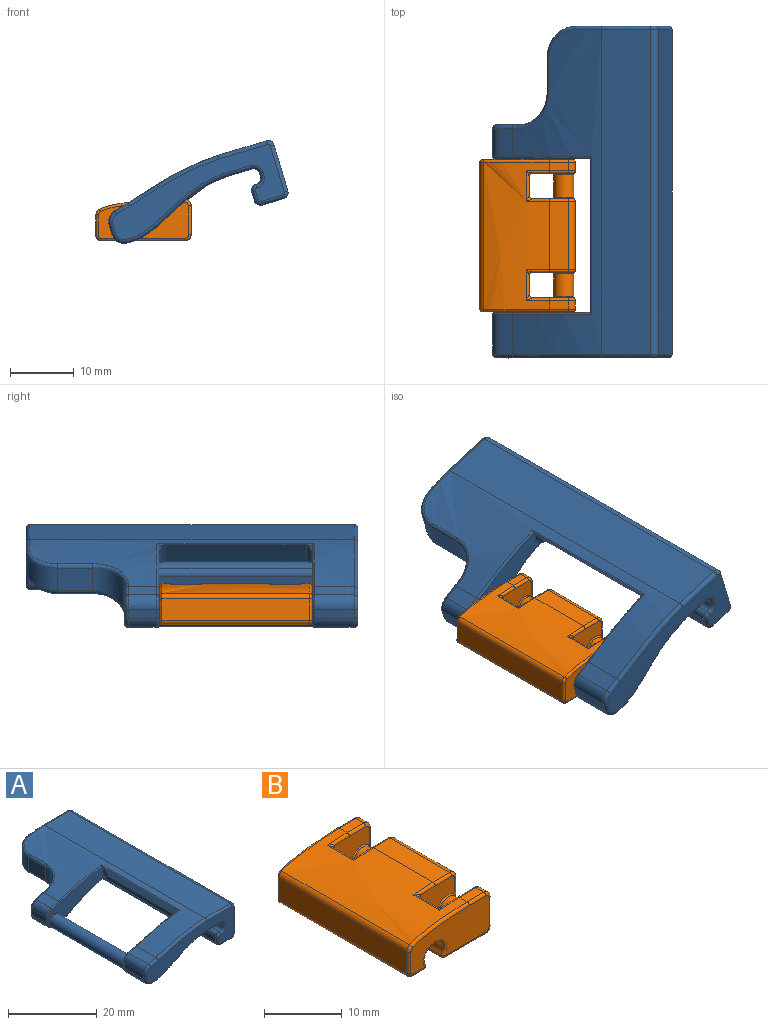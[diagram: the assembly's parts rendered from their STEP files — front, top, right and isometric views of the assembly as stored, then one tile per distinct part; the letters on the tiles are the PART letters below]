
ASSEMBLY  parts=2 mates=1
PART A: 118 faces, bbox 30x52.3x9.5 mm
  f0: plane 2.15x0.64mm, normal (-1,0,0), area 0.4mm2, adj f21,f24,f84,f85
  f1: extruded ~51.05x15.64mm, area 359.3mm2, adj f3,f12,f13,f38,f39,f41,f43,f45
  f2: extruded ~51.05x17mm, area 362.6mm2, adj f4,f15,f16,f50,f52,f54,f56,f58
  f3: plane 4.5x2.38mm, normal (-0.26,0,0.97), area 11.1mm2, adj f1,f5,f40,f88
  f4: plane 4.69x1mm, normal (0,0,-1), area 4.6mm2, adj f2,f6,f48,f98
  f5: cylinder r=2mm len=4.5mm, axis (0,-1,0), area 11.8mm2, adj f3,f17,f42,f90
  f6: cylinder r=2mm len=4.63mm, axis (0,1,0), area 14.2mm2, adj f4,f17,f46,f94,f96
  f7: plane 12.9x8.3mm, normal (0,1,0), area 50.6mm2, adj f37,f45,f47,f49,f51,f53,f55,f57
  f8: plane 51.05x0.5mm, normal (-1,0,0), area 25.5mm2, adj f29,f33,f64,f81
  f9: plane 51.05x1.4mm, normal (-1,0,0), area 71.5mm2, adj f28,f30,f59,f80
  f10: plane 51.05x3.5mm, normal (0,0,-1), area 178.7mm2, adj f30,f31,f55,f76
  f11: plane 51.05x7.5mm, normal (1,0,0), area 382.9mm2, adj f31,f32,f51,f72
  f12: plane 51.05x8mm, normal (0,0,1), area 408.4mm2, adj f1,f32,f47,f68
  f13: plane 6.25x2.38mm, normal (-0.26,0,0.97), area 15.4mm2, adj f1,f18,f65,f87
  f14: plane 6.25x1.47mm, normal (-1,0,0), area 9.2mm2, adj f18,f19,f69,f91
  f15: plane 6.44x1mm, normal (0,0,-1), area 6.4mm2, adj f2,f19,f73,f97
  f16: plane 51.05x4mm, normal (0,0,-1), area 204.2mm2, adj f2,f33,f60,f77
  f17: plane 4.5x1.47mm, normal (-1,0,0), area 6.6mm2, adj f5,f6,f44,f92
  f18: cylinder r=2mm len=6.25mm, axis (0,-1,0), area 16.4mm2, adj f13,f14,f67,f89
  f19: cylinder r=2mm len=6.38mm, axis (0,1,0), area 19.7mm2, adj f14,f15,f71,f93,f95
  f20: plane 2.15x0.64mm, normal (-1,0,0), area 0.4mm2, adj f22,f25,f84,f86
  f21: plane 17.65x8.41mm, normal (0,1,0), area 66.1mm2, adj f0,f24,f85,f87,f89,f91,f93,f101
  f22: plane 17.65x8.41mm, normal (0,-1,0), area 66.1mm2, adj f20,f25,f86,f88,f90,f92,f94,f102
  f23: plane 22.2x3.18mm, normal (-0.9,0,-0.43), area 78.3mm2, adj f24,f25,f84,f105
  f24: cylinder r=1mm len=3.61mm, axis (-0.43,0,0.9), area 4mm2, adj f0,f21,f23,f84,f103
  f25: cylinder r=1mm len=3.61mm, axis (-0.43,0,0.9), area 4mm2, adj f20,f22,f23,f84,f104
  f26: cylinder r=1.7mm len=24.12mm, axis (0,-1,0), area 255.7mm2, adj f106,f107,f108,f109,f110,f111,f112,f113
  f27: plane 27.3x8.3mm, normal (0,-1,0), area 108.1mm2, adj f65,f66,f67,f68,f69,f70,f71,f72
  f28: cylinder r=1mm len=51.05mm, axis (0,1,0), area 80.2mm2, adj f9,f29,f61,f82
  f29: cylinder r=1mm len=51.05mm, axis (0,-1,0), area 80.2mm2, adj f8,f28,f63,f83
  f30: cylinder r=1mm len=51.05mm, axis (0,1,0), area 80.2mm2, adj f9,f10,f57,f78
  f31: cylinder r=1mm len=51.05mm, axis (0,1,0), area 80.2mm2, adj f10,f11,f53,f74
  f32: cylinder r=1mm len=51.05mm, axis (0,1,0), area 80.2mm2, adj f11,f12,f49,f70
  f33: cylinder r=1mm len=51.05mm, axis (0,-1,0), area 80.2mm2, adj f8,f16,f62,f79
  f34: plane 5.13x4.4mm, normal (0,1,0), area 19mm2, adj f36,f38,f40,f42,f44,f46,f48,f50
  f35: plane 5.5x3.74mm, normal (-1,0,0), area 20.5mm2, adj f36,f37,f41,f54
  f36: cylinder r=5mm len=6.31mm, axis (0,0,-1), area 33.4mm2, adj f34,f35,f39,f52
  f37: cylinder r=5mm len=5mm, axis (0,0,-1), area 25.6mm2, adj f7,f35,f43,f56
  f38: bspline ~5.06x1.94mm, area 1mm2, adj f1,f34,f39,f40
  f39: bspline ~6.9x6.82mm, area 7.1mm2, adj f1,f36,f38,f41
  f40: cylinder r=0.6mm len=2.54mm, axis (-0.97,0,-0.26), area 2.3mm2, adj f3,f34,f38,f42
  f41: cylinder r=0.6mm len=5.5mm, axis (0,1,0), area 4.4mm2, adj f1,f35,f39,f43
  f42: torus R=1.4mm, axis (0,1,0), area 2.2mm2, adj f5,f34,f40,f44
  f43: bspline ~6.11x6.1mm, area 6.5mm2, adj f1,f37,f41,f45
  f44: cylinder r=0.6mm len=1.47mm, axis (0,0,1), area 1.4mm2, adj f17,f34,f42,f46
  f45: bspline ~11.49x1.65mm, area 4.3mm2, adj f1,f7,f43,f47
  f46: torus R=1.4mm, axis (0,1,0), area 2.6mm2, adj f6,f34,f44,f48
  f47: cylinder r=0.6mm len=8mm, axis (-1,0,0), area 7.5mm2, adj f7,f12,f45,f49
  f48: cylinder r=0.6mm len=1mm, axis (1,0,0), area 0.9mm2, adj f4,f34,f46,f50
  f49: torus R=0.4mm, axis (0,-1,0), area 1.2mm2, adj f7,f32,f47,f51
  f50: bspline ~7.83x1.34mm, area 2mm2, adj f2,f34,f48,f52
  f51: cylinder r=0.6mm len=7.5mm, axis (0,0,1), area 7.1mm2, adj f7,f11,f49,f53
  f52: bspline ~6.83x6.75mm, area 9.6mm2, adj f2,f36,f50,f54
  f53: torus R=0.4mm, axis (0,-1,0), area 1.2mm2, adj f7,f31,f51,f55
  f54: cylinder r=0.6mm len=5.5mm, axis (0,1,0), area 6.7mm2, adj f2,f35,f52,f56
  f55: cylinder r=0.6mm len=3.5mm, axis (1,0,0), area 3.3mm2, adj f7,f10,f53,f57
  f56: bspline ~6.23x6.14mm, area 8.6mm2, adj f2,f37,f54,f58
  f57: torus R=0.4mm, axis (0,-1,0), area 1.2mm2, adj f7,f30,f55,f59
  f58: bspline ~9.53x1.81mm, area 4.7mm2, adj f2,f7,f56,f60
  f59: cylinder r=0.6mm len=1.4mm, axis (0,0,-1), area 1.3mm2, adj f7,f9,f57,f61
  f60: cylinder r=0.6mm len=4mm, axis (1,0,0), area 3.8mm2, adj f7,f16,f58,f62
  f61: torus R=0.4mm, axis (0,-1,0), area 1.2mm2, adj f7,f28,f59,f63
  f62: torus R=1.6mm, axis (0,-1,0), area 1.8mm2, adj f7,f33,f60,f64
  f63: torus R=1.6mm, axis (0,-1,0), area 1.8mm2, adj f7,f29,f61,f64
  f64: cylinder r=0.6mm len=0.6mm, axis (0,0,-1), area 0.5mm2, adj f7,f8,f62,f63
  f65: cylinder r=0.6mm len=2.54mm, axis (0.97,0,0.26), area 2.3mm2, adj f13,f27,f66,f67
  f66: bspline ~22.43x4.59mm, area 15mm2, adj f1,f27,f65,f68
  f67: torus R=1.4mm, axis (0,-1,0), area 2.2mm2, adj f18,f27,f65,f69
  f68: cylinder r=0.6mm len=8mm, axis (1,0,0), area 7.5mm2, adj f12,f27,f66,f70
  f69: cylinder r=0.6mm len=1.47mm, axis (0,0,1), area 1.4mm2, adj f14,f27,f67,f71
  f70: torus R=0.4mm, axis (0,-1,0), area 1.2mm2, adj f27,f32,f68,f72
  f71: torus R=1.4mm, axis (0,-1,0), area 2.6mm2, adj f19,f27,f69,f73
  f72: cylinder r=0.6mm len=7.5mm, axis (0,0,-1), area 7.1mm2, adj f11,f27,f70,f74
  f73: cylinder r=0.6mm len=1mm, axis (-1,0,0), area 0.9mm2, adj f15,f27,f71,f75
  f74: torus R=0.4mm, axis (0,-1,0), area 1.2mm2, adj f27,f31,f72,f76
  f75: bspline ~23.39x6.15mm, area 17mm2, adj f2,f27,f73,f77
  f76: cylinder r=0.6mm len=3.5mm, axis (-1,0,0), area 3.3mm2, adj f10,f27,f74,f78
  f77: cylinder r=0.6mm len=4mm, axis (-1,0,0), area 3.8mm2, adj f16,f27,f75,f79
  f78: torus R=0.4mm, axis (0,-1,0), area 1.2mm2, adj f27,f30,f76,f80
  f79: torus R=1.6mm, axis (0,-1,0), area 1.8mm2, adj f27,f33,f77,f81
  f80: cylinder r=0.6mm len=1.4mm, axis (0,0,1), area 1.3mm2, adj f9,f27,f78,f82
  f81: cylinder r=0.6mm len=0.6mm, axis (0,0,1), area 0.5mm2, adj f8,f27,f79,f83
  f82: torus R=0.4mm, axis (0,-1,0), area 1.2mm2, adj f27,f28,f80,f83
  f83: torus R=1.6mm, axis (0,-1,0), area 1.8mm2, adj f27,f29,f81,f82
  f84: cylinder r=0.3mm len=24.8mm, axis (0,1,0), area 8.4mm2, adj f0,f1,f20,f23,f24,f25,f85,f86
  f85: bspline ~18.1x4.27mm, area 6.6mm2, adj f0,f1,f21,f84,f87
  f86: bspline ~18.1x4.27mm, area 6.6mm2, adj f1,f20,f22,f84,f88
  f87: cylinder r=0.3mm len=2.46mm, axis (-0.97,0,-0.26), area 1.2mm2, adj f13,f21,f85,f89
  f88: cylinder r=0.3mm len=2.46mm, axis (0.97,0,0.26), area 1.2mm2, adj f3,f22,f86,f90
  f89: torus R=1.7mm, axis (0,-1,0), area 1.2mm2, adj f18,f21,f87,f91
  f90: torus R=1.7mm, axis (0,-1,0), area 1.2mm2, adj f5,f22,f88,f92
  f91: cylinder r=0.3mm len=1.47mm, axis (0,0,-1), area 0.7mm2, adj f14,f21,f89,f93
  f92: cylinder r=0.3mm len=1.47mm, axis (0,0,1), area 0.7mm2, adj f17,f22,f90,f94
  f93: torus R=1.7mm, axis (0,-1,0), area 0.8mm2, adj f19,f21,f91,f95,f113
  f94: torus R=1.7mm, axis (0,-1,0), area 0.8mm2, adj f6,f22,f92,f96,f107
  f95: bspline ~1.38x0.75mm, area 0.4mm2, adj f19,f93,f97,f115
  f96: bspline ~1.38x0.75mm, area 0.4mm2, adj f6,f94,f98,f109
  f97: bspline ~1.28x0.3mm, area 0.2mm2, adj f15,f95,f99,f117
  f98: bspline ~1.36x0.3mm, area 0.2mm2, adj f4,f96,f100,f111
  f99: bspline ~0.53x0.33mm, area 0.1mm2, adj f2,f97,f101,f116
  f100: bspline ~0.53x0.33mm, area 0.1mm2, adj f2,f98,f102,f110
  f101: bspline ~16.63x5.79mm, area 7.4mm2, adj f2,f21,f99,f103,f114
  f102: bspline ~16.63x5.79mm, area 7.4mm2, adj f2,f22,f100,f104,f108
  f103: bspline ~1.65x1.37mm, area 0.7mm2, adj f2,f24,f101,f105
  f104: bspline ~1.65x1.58mm, area 0.7mm2, adj f2,f25,f102,f105
  f105: cylinder r=0.3mm len=22.2mm, axis (0,1,0), area 7.9mm2, adj f2,f23,f103,f104
  f106: torus R=1.85mm, axis (0,-1,0), area 1.8mm2, adj f22,f26,f107,f108
  f107: bspline ~1.22x0.86mm, area 0.1mm2, adj f26,f94,f106,f109
  f108: bspline ~0.43x0.3mm, area 0.1mm2, adj f26,f102,f106,f110
  f109: bspline ~1.14x0.61mm, area 0.1mm2, adj f26,f96,f107,f111
  f110: bspline ~0.33x0.18mm, area 0mm2, adj f26,f100,f108,f111
  f111: bspline ~1.32x0.23mm, area 0.1mm2, adj f26,f98,f109,f110
  f112: torus R=1.85mm, axis (0,-1,0), area 1.8mm2, adj f21,f26,f113,f114
  f113: bspline ~1.22x0.86mm, area 0.1mm2, adj f26,f93,f112,f115
  f114: bspline ~0.43x0.3mm, area 0.1mm2, adj f26,f101,f112,f116
  f115: bspline ~1.14x0.61mm, area 0.1mm2, adj f26,f95,f113,f117
  f116: bspline ~0.33x0.18mm, area 0mm2, adj f26,f99,f114,f117
  f117: bspline ~1.21x0.2mm, area 0.1mm2, adj f26,f97,f115,f116
PART B: 149 faces, bbox 15.2x24x6.7 mm
  f0: plane 14.2x5.7mm, normal (0,-1,0), area 64.1mm2, adj f30,f31,f32,f33,f34,f36,f37,f38
  f1: plane 14.2x5.7mm, normal (0,1,0), area 64.1mm2, adj f42,f43,f44,f45,f46,f48,f49,f50
  f2: plane 6.3x5.7mm, normal (0,1,0), area 26.9mm2, adj f76,f77,f78,f80,f92,f99,f100,f118
  f3: plane 6.3x5.7mm, normal (0,-1,0), area 26.9mm2, adj f81,f83,f85,f87,f96,f103,f104,f126
  f4: plane 6.3x5.7mm, normal (0,-1,0), area 26.9mm2, adj f54,f55,f57,f59,f71,f107,f108,f134
  f5: plane 6.3x5.7mm, normal (0,1,0), area 26.9mm2, adj f58,f60,f62,f64,f75,f111,f112,f142
  f6: plane 23.2x7.47mm, normal (0,0,-1), area 110.3mm2, adj f12,f16,f22,f26,f33,f45,f69,f71
  f7: plane 4.5x1.45mm, normal (1,0,0), area 6.3mm2, adj f15,f16,f42,f59,f61
  f8: plane 23.2x2.37mm, normal (0,0,-1), area 55mm2, adj f27,f41,f53,f147
  f9: plane 10.8x3mm, normal (0,0,1), area 32.4mm2, adj f10,f11,f60,f83
  f10: extruded ~23.2x10.46mm, area 211.7mm2, adj f9,f14,f18,f20,f36,f48,f54,f56
  f11: cylinder r=1mm len=10.8mm, axis (0,1,0), area 17mm2, adj f9,f13,f62,f85
  f12: cylinder r=1mm len=10.8mm, axis (0,1,0), area 17mm2, adj f6,f13,f68,f70,f72,f91,f93,f95
  f13: plane 10.91x4.5mm, normal (1,0,0), area 48.7mm2, adj f11,f12,f64,f66,f87,f89
  f14: plane 3x1.4mm, normal (0,0,1), area 4.2mm2, adj f10,f15,f46,f55
  f15: cylinder r=1mm len=1.4mm, axis (0,1,0), area 2.2mm2, adj f7,f14,f44,f57
  f16: cylinder r=1mm len=1.4mm, axis (0,1,0), area 2.2mm2, adj f6,f7,f43,f63,f65,f67
  f17: plane 4.5x1.45mm, normal (1,0,0), area 6.3mm2, adj f21,f22,f30,f80,f82
  f18: plane 3x1.4mm, normal (0,0,1), area 4.2mm2, adj f10,f21,f34,f76
  f19: plane 23.2x3.37mm, normal (-1,0,0), area 78.2mm2, adj f20,f40,f52,f147
  f20: cylinder r=1mm len=23.2mm, axis (0,1,0), area 25.4mm2, adj f10,f19,f38,f50
  f21: cylinder r=1mm len=1.4mm, axis (0,1,0), area 2.2mm2, adj f17,f18,f32,f78
  f22: cylinder r=1mm len=1.4mm, axis (0,1,0), area 2.2mm2, adj f6,f17,f31,f84,f86,f88
  f23: plane 5.51x3mm, normal (1,0,0), area 16.5mm2, adj f79,f94,f99,f103
  f24: plane 5.51x3mm, normal (1,0,0), area 16.5mm2, adj f56,f73,f107,f111
  f25: cylinder r=1.75mm len=23.2mm, axis (0,-1,0), area 173.5mm2, adj f26,f27,f37,f49
  f26: cylinder r=0.3mm len=23.2mm, axis (0,-1,0), area 14.9mm2, adj f6,f25,f35,f47
  f27: cylinder r=0.3mm len=23.2mm, axis (0,-1,0), area 14.9mm2, adj f8,f25,f39,f51
  f28: cylinder r=1.6mm len=3.83mm, axis (0,-1,0), area 36.8mm2, adj f130,f131,f132,f133,f134,f135,f136,f137
  f29: cylinder r=1.6mm len=3.83mm, axis (0,-1,0), area 36.8mm2, adj f114,f115,f116,f117,f118,f119,f120,f121
  f30: cylinder r=0.4mm len=4.5mm, axis (0,0,-1), area 2.8mm2, adj f0,f17,f31,f32
  f31: torus R=0.6mm, axis (0,-1,0), area 0.8mm2, adj f0,f22,f30,f33
  f32: torus R=0.6mm, axis (0,-1,0), area 0.8mm2, adj f0,f21,f30,f34
  f33: cylinder r=0.4mm len=7.47mm, axis (-1,0,0), area 4.6mm2, adj f0,f6,f31,f35
  f34: cylinder r=0.4mm len=3mm, axis (1,0,0), area 1.9mm2, adj f0,f18,f32,f36
  f35: bspline ~0.72x0.59mm, area 0.2mm2, adj f26,f33,f37
  f36: bspline ~12.18x1.99mm, area 6.6mm2, adj f0,f10,f34,f38
  f37: torus R=2.15mm, axis (0,-1,0), area 5mm2, adj f0,f25,f35,f39
  f38: torus R=0.6mm, axis (0,-1,0), area 0.6mm2, adj f0,f20,f36,f40
  f39: bspline ~0.72x0.59mm, area 0.2mm2, adj f27,f37,f41
  f40: cylinder r=0.4mm len=3.37mm, axis (0,0,1), area 2.1mm2, adj f0,f19,f38,f146
  f41: cylinder r=0.4mm len=2.37mm, axis (-1,0,0), area 1.4mm2, adj f0,f8,f39,f146
  f42: cylinder r=0.4mm len=4.5mm, axis (0,0,1), area 2.8mm2, adj f1,f7,f43,f44
  f43: torus R=0.6mm, axis (0,-1,0), area 0.8mm2, adj f1,f16,f42,f45
  f44: torus R=0.6mm, axis (0,-1,0), area 0.8mm2, adj f1,f15,f42,f46
  f45: cylinder r=0.4mm len=7.47mm, axis (1,0,0), area 4.6mm2, adj f1,f6,f43,f47
  f46: cylinder r=0.4mm len=3mm, axis (-1,0,0), area 1.9mm2, adj f1,f14,f44,f48
  f47: bspline ~0.72x0.59mm, area 0.2mm2, adj f26,f45,f49
  f48: bspline ~12.18x1.99mm, area 6.6mm2, adj f1,f10,f46,f50
  f49: torus R=2.15mm, axis (0,-1,0), area 5mm2, adj f1,f25,f47,f51
  f50: torus R=0.6mm, axis (0,-1,0), area 0.6mm2, adj f1,f20,f48,f52
  f51: bspline ~0.72x0.59mm, area 0.2mm2, adj f27,f49,f53
  f52: cylinder r=0.4mm len=3.37mm, axis (0,0,-1), area 2.1mm2, adj f1,f19,f50,f148
  f53: cylinder r=0.4mm len=2.37mm, axis (1,0,0), area 1.4mm2, adj f1,f8,f51,f148
  f54: bspline ~6.15x0.69mm, area 2mm2, adj f4,f10,f55,f109
  f55: cylinder r=0.4mm len=3mm, axis (1,0,0), area 1.9mm2, adj f4,f14,f54,f57
  f56: cylinder r=0.4mm len=4.8mm, axis (0,1,0), area 2.4mm2, adj f10,f24,f108,f109,f112,f113
  f57: torus R=0.6mm, axis (0,1,0), area 0.8mm2, adj f4,f15,f55,f59
  f58: bspline ~6.15x0.69mm, area 2mm2, adj f5,f10,f60,f113
  f59: cylinder r=0.4mm len=2.98mm, axis (0,0,1), area 1.8mm2, adj f4,f7,f57,f61,f132
  f60: cylinder r=0.4mm len=3mm, axis (-1,0,0), area 1.9mm2, adj f5,f9,f58,f62
  f61: bspline ~1.89x0.49mm, area 0.6mm2, adj f7,f59,f63,f130
  f62: torus R=0.6mm, axis (0,1,0), area 0.8mm2, adj f5,f11,f60,f64
  f63: bspline ~0.46x0.45mm, area 0mm2, adj f16,f61,f65,f131
  f64: cylinder r=0.4mm len=2.98mm, axis (0,0,-1), area 1.8mm2, adj f5,f13,f62,f66,f140
  f65: torus R=0.6mm, axis (0,1,0), area 0.7mm2, adj f16,f63,f67,f133
  f66: bspline ~1.89x0.49mm, area 0.6mm2, adj f13,f64,f68,f138
  f67: bspline ~0.44x0.43mm, area 0mm2, adj f16,f65,f69,f135
  f68: bspline ~0.46x0.45mm, area 0mm2, adj f12,f66,f70,f139
  f69: bspline ~2x0.47mm, area 0.6mm2, adj f6,f67,f71,f137
  f70: torus R=0.6mm, axis (0,1,0), area 0.7mm2, adj f12,f68,f72,f141
  f71: cylinder r=0.4mm len=4.94mm, axis (-1,0,0), area 2.7mm2, adj f4,f6,f69,f106,f136
  f72: bspline ~0.44x0.43mm, area 0mm2, adj f12,f70,f74,f143
  f73: cylinder r=0.4mm len=4.8mm, axis (0,-1,0), area 2.5mm2, adj f6,f24,f106,f110
  f74: bspline ~2x0.47mm, area 0.6mm2, adj f6,f72,f75,f145
  f75: cylinder r=0.4mm len=4.94mm, axis (1,0,0), area 2.7mm2, adj f5,f6,f74,f110,f144
  f76: cylinder r=0.4mm len=3mm, axis (-1,0,0), area 1.9mm2, adj f2,f18,f77,f78
  f77: bspline ~6.15x0.69mm, area 2mm2, adj f2,f10,f76,f101
  f78: torus R=0.6mm, axis (0,-1,0), area 0.8mm2, adj f2,f21,f76,f80
  f79: cylinder r=0.4mm len=4.8mm, axis (0,1,0), area 2.4mm2, adj f10,f23,f100,f101,f104,f105
  f80: cylinder r=0.4mm len=2.98mm, axis (0,0,1), area 1.8mm2, adj f2,f17,f78,f82,f120
  f81: bspline ~6.15x0.69mm, area 2mm2, adj f3,f10,f83,f105
  f82: bspline ~1.89x0.49mm, area 0.6mm2, adj f17,f80,f84,f121
  f83: cylinder r=0.4mm len=3mm, axis (1,0,0), area 1.9mm2, adj f3,f9,f81,f85
  f84: bspline ~0.44x0.43mm, area 0mm2, adj f22,f82,f86,f119
  f85: torus R=0.6mm, axis (0,-1,0), area 0.8mm2, adj f3,f11,f83,f87
  f86: torus R=0.6mm, axis (0,-1,0), area 0.7mm2, adj f22,f84,f88,f117
  f87: cylinder r=0.4mm len=2.98mm, axis (0,0,-1), area 1.8mm2, adj f3,f13,f85,f89,f128
  f88: bspline ~0.46x0.45mm, area 0mm2, adj f22,f86,f90,f115
  f89: bspline ~1.89x0.49mm, area 0.6mm2, adj f13,f87,f91,f129
  f90: bspline ~2x0.47mm, area 0.6mm2, adj f6,f88,f92,f114
  f91: bspline ~0.44x0.43mm, area 0mm2, adj f12,f89,f93,f127
  f92: cylinder r=0.4mm len=4.94mm, axis (1,0,0), area 2.7mm2, adj f2,f6,f90,f98,f116
  f93: torus R=0.6mm, axis (0,-1,0), area 0.7mm2, adj f12,f91,f95,f125
  f94: cylinder r=0.4mm len=4.8mm, axis (0,-1,0), area 2.5mm2, adj f6,f23,f98,f102
  f95: bspline ~0.46x0.45mm, area 0mm2, adj f12,f93,f97,f123
  f96: cylinder r=0.4mm len=4.94mm, axis (-1,0,0), area 2.7mm2, adj f3,f6,f97,f102,f124
  f97: bspline ~2x0.47mm, area 0.6mm2, adj f6,f95,f96,f122
  f98: bspline ~0.9x0.9mm, area 0.2mm2, adj f92,f94,f99
  f99: cylinder r=0.5mm len=5.51mm, axis (0,0,1), area 4.3mm2, adj f2,f23,f98,f100
  f100: torus R=0.9mm, axis (0,-1,0), area 0mm2, adj f2,f79,f99,f101
  f101: bspline ~0.93x0.9mm, area 0.2mm2, adj f77,f79,f100
  f102: bspline ~0.9x0.9mm, area 0.2mm2, adj f94,f96,f103
  f103: cylinder r=0.5mm len=5.51mm, axis (0,0,-1), area 4.3mm2, adj f3,f23,f102,f104
  f104: torus R=0.9mm, axis (0,-1,0), area 0mm2, adj f3,f79,f103,f105
  f105: bspline ~0.93x0.9mm, area 0.2mm2, adj f79,f81,f104
  f106: bspline ~0.9x0.9mm, area 0.2mm2, adj f71,f73,f107
  f107: cylinder r=0.5mm len=5.51mm, axis (0,0,-1), area 4.3mm2, adj f4,f24,f106,f108
  f108: torus R=0.9mm, axis (0,1,0), area 0mm2, adj f4,f56,f107,f109
  f109: bspline ~0.93x0.9mm, area 0.2mm2, adj f54,f56,f108
  f110: bspline ~0.9x0.9mm, area 0.2mm2, adj f73,f75,f111
  f111: cylinder r=0.5mm len=5.51mm, axis (0,0,1), area 4.3mm2, adj f5,f24,f110,f112
  f112: torus R=0.9mm, axis (0,1,0), area 0mm2, adj f5,f56,f111,f113
  f113: bspline ~0.93x0.9mm, area 0.2mm2, adj f56,f58,f112
  f114: bspline ~1.91x0.31mm, area 0.3mm2, adj f29,f90,f115,f116
  f115: bspline ~0.23x0.21mm, area 0mm2, adj f29,f88,f114,f117
  f116: bspline ~0.79x0.44mm, area 0.1mm2, adj f29,f92,f114,f118
  f117: bspline ~0.88x0.83mm, area 0.3mm2, adj f29,f86,f115,f119
  f118: torus R=1.8mm, axis (0,-1,0), area 1.7mm2, adj f2,f29,f116,f120
  f119: bspline ~0.2x0.16mm, area 0mm2, adj f29,f84,f117,f121
  f120: bspline ~0.67x0.45mm, area 0.1mm2, adj f29,f80,f118,f121
  f121: bspline ~1.76x0.29mm, area 0.3mm2, adj f29,f82,f119,f120
  f122: bspline ~1.91x0.31mm, area 0.3mm2, adj f29,f97,f123,f124
  f123: bspline ~0.23x0.21mm, area 0mm2, adj f29,f95,f122,f125
  f124: bspline ~0.79x0.44mm, area 0.1mm2, adj f29,f96,f122,f126
  f125: bspline ~0.88x0.83mm, area 0.3mm2, adj f29,f93,f123,f127
  f126: torus R=1.8mm, axis (0,-1,0), area 1.7mm2, adj f3,f29,f124,f128
  f127: bspline ~0.2x0.16mm, area 0mm2, adj f29,f91,f125,f129
  f128: bspline ~0.67x0.45mm, area 0.1mm2, adj f29,f87,f126,f129
  f129: bspline ~1.68x0.29mm, area 0.3mm2, adj f29,f89,f127,f128
  f130: bspline ~1.76x0.28mm, area 0.3mm2, adj f28,f61,f131,f132
  f131: bspline ~0.2x0.17mm, area 0mm2, adj f28,f63,f130,f133
  f132: bspline ~0.52x0.35mm, area 0.1mm2, adj f28,f59,f130,f134
  f133: bspline ~0.88x0.84mm, area 0.3mm2, adj f28,f65,f131,f135
  f134: torus R=1.8mm, axis (0,1,0), area 1.7mm2, adj f4,f28,f132,f136
  f135: bspline ~0.2x0.18mm, area 0mm2, adj f28,f67,f133,f137
  f136: bspline ~0.65x0.46mm, area 0.1mm2, adj f28,f71,f134,f137
  f137: bspline ~1.81x0.31mm, area 0.3mm2, adj f28,f69,f135,f136
  f138: bspline ~1.76x0.28mm, area 0.3mm2, adj f28,f66,f139,f140
  f139: bspline ~0.2x0.17mm, area 0mm2, adj f28,f68,f138,f141
  f140: bspline ~0.52x0.35mm, area 0.1mm2, adj f28,f64,f138,f142
  f141: bspline ~0.88x0.84mm, area 0.3mm2, adj f28,f70,f139,f143
  f142: torus R=1.8mm, axis (0,1,0), area 1.7mm2, adj f5,f28,f140,f144
  f143: bspline ~0.2x0.18mm, area 0mm2, adj f28,f72,f141,f145
  f144: bspline ~0.65x0.46mm, area 0.1mm2, adj f28,f75,f142,f145
  f145: bspline ~1.81x0.31mm, area 0.3mm2, adj f28,f74,f143,f144
  f146: torus R=0.3mm, axis (0,-1,0), area 0.5mm2, adj f0,f40,f41,f147
  f147: cylinder r=0.7mm len=23.2mm, axis (0,1,0), area 25.5mm2, adj f8,f19,f146,f148
  f148: torus R=0.3mm, axis (0,-1,0), area 0.5mm2, adj f1,f52,f53,f147
PLACE A rot(axis=(0,-1,0),16.6deg) t=(25.23,0,5.34)mm
PLACE B at identity fixed
MATE revolute A.f26 <-> B.f25  axis (0,-1,0) through (4.8,0,1.4)mm
